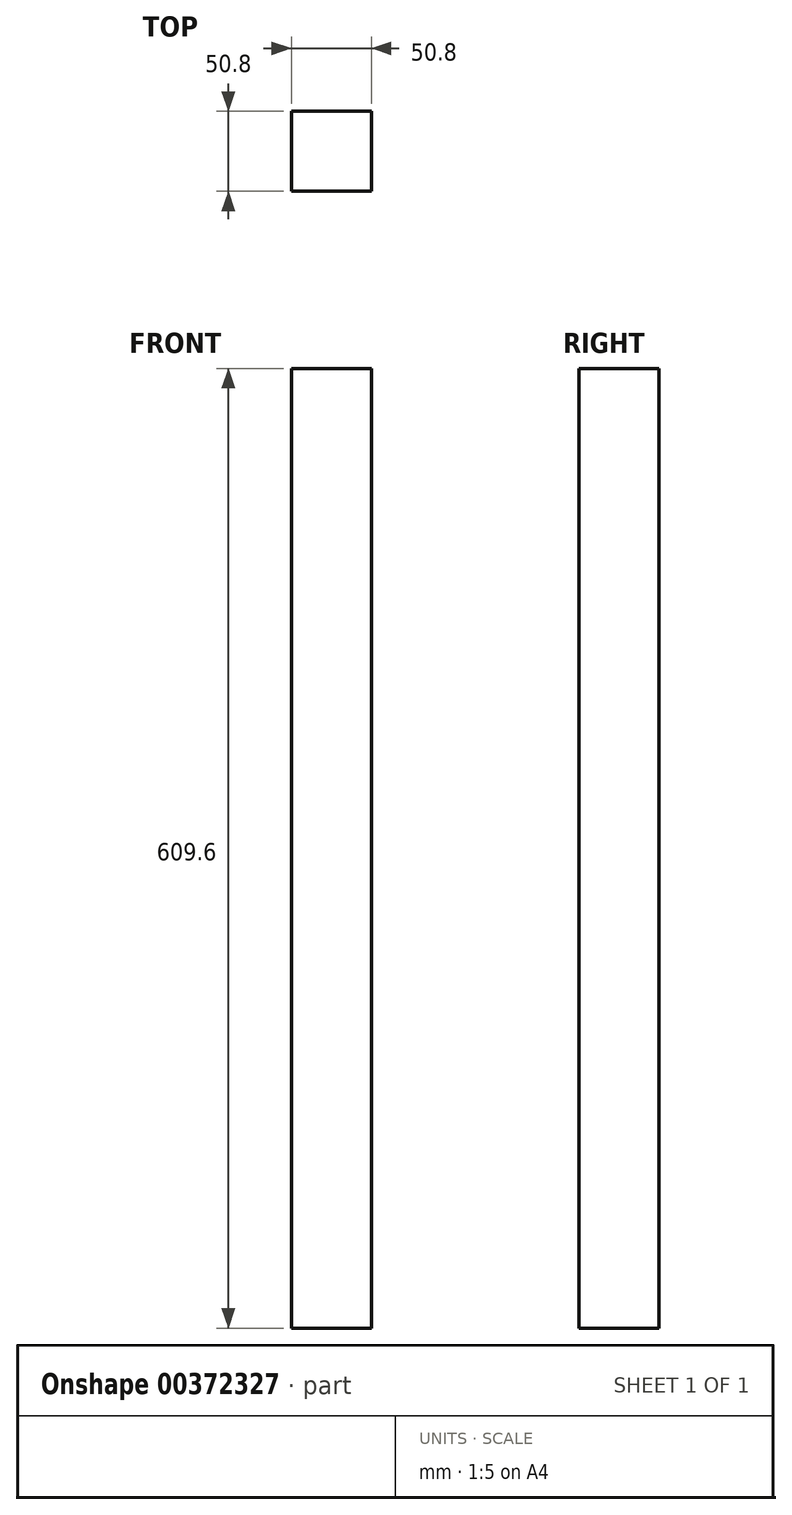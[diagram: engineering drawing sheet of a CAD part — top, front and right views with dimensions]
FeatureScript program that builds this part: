
annotation { "Feature Type Name" : "Feature", "Feature Type Description" : "" }
export const myFeature = defineFeature(function(context is Context, id is Id, definition is map)
    precondition{}
    {
        {
            var Q0;
            Q0=qCreatedBy(makeId("Top.planeOp"),FACE);
            var sketch = newSketch(context, id + "F0", { "sketchPlane" : qUnion([Q0])});
            skLineSegment(sketch, "E0.bottom", {"start": v(0, 0) * mm, "end": v(50.8, 0) * mm});
            skLineSegment(sketch, "E0.top", {"start": v(0, 50.8) * mm, "end": v(50.8, 50.8) * mm});
            skLineSegment(sketch, "E0.left", {"start": v(0, 0) * mm, "end": v(0, 50.8) * mm});
            skLineSegment(sketch, "E0.right", {"start": v(50.8, 0) * mm, "end": v(50.8, 50.8) * mm});
            skSolve(sketch);
        }
        {
            var Q0;
            Q0 = qSketchRegion(id + "F0", true);
            extrude(context, id + "F1", {"entities" : qUnion([Q0]), "depth" : 609.6 * mm});
        }
    });
